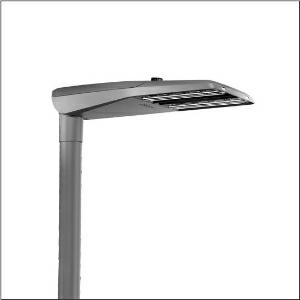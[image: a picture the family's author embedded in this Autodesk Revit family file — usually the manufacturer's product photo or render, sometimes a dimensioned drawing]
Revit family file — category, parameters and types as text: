
# Revit family: streetlight_sl_11_iq_midi___st1_2a_5xc3a41u08me_4bff
name_source: partatom
category: Lighting Fixtures
units: mm (PartAtom-declared; Revit-internal decimal feet)

## family parameters
Cut with Voids When Loaded = No
Host = Face
Light Source = No
Part Type = Normal
Room Calculation Point = No
Round Connector Dimension = Use Diameter
Shared = No

## types (1)
- --- (1 x LED, 18900 lm, 122.6 W, 4000K)
    Apparent Load = 123 VA
    CIE Flux Codes = 32 70 96 100 100
    Color Rendering = 70
    Color Temperature = 4000K
    Default Elevation = 1800 mm
    Description = Streetlight SL 11 iQ midi, mast luminaire, primary light control with 3 zone facetted reflector, of plastic, silver coated, highly specular, primary optical cover: cover, of PMMA, transparent, light distribution: ST1.2a, light emission: direct distribution, primary light characteristic: asymmetric, installation type: post-top, side-entry, lamps: LED, High Power LED, rated values: 18.900lm | 122,6W | 154,2lm/W (begin service life); end service life: 18.900lm | 130,2W; at 50% lumin. flux: 9.450lm | 56,3W | 167,9lm/W, colour temperature: 4000K, colour rendering: CRI > 70, light colour: 740, light setting 1 begin service life: 100% | 18.900lm | 122,6W | 154,2lm/W | 4.000K, light setting 1 end service life: 130,2W, further light settings possible, control: pre-setting: logarithmic dimming characteristic, Street-Remote, Auto-Match, Temp-Guard, Lumen-Switch, Night-Set, Smart-Wire, Light-Fading, Desk-Remote (wireless, voltage-free reading and setting of iQ features in the workshop via application-optimized NFC function/RFID function), optimised constant luminous flux control (CLO 2.0), with cable H07RN-F 5x 1.5mm², mains connection: 230..240V, AC, 50/60Hz, connection cable pre-assembled, cable length: 12,5m, luminaire housing, of diecast aluminium, powder-coated, Siteco® metallic grey (DB 702S), please order mast flange separately, inclination adjustable without tools: 0°, 5°, 10°, 15° (post-top) | 0°, -5°, -10°, -15° (side-entry), sealing non-destructively replaceable, multi-level sealing system, length: 780mm, width: 376mm, height: 118mm, mast flange for spigot size: 42mm (side-entry): 5XC10008XM4, 60/48mm (side-entry/post-top): 5XC10108XM2, 76/60mm (side-entry/post-top): 5XC10108XM1, equipment: Power, Smart Interface below, protection rating (complete): IP66, insulation class (complete): insulation class II (safety insulation), certification: CE, ENEC, ENEC+, VDE, UKCA, impact resistance: IK10, permissible operating ambient temperature for outdoor applications: -25..+50°C, standard-compliant lighting for roads and squares, Environmental Product Declaration (EPD) tested and certified by an independent institute, packaging unit: 1 piece

Light Distribution: ST1.2a
    Height = 118 mm
    Lamp = 1 x LED
    Lamp Light Flux = 18900 lm
    Lamp Power = 122.6 W
    Lamp count = 1
    Length = 780 mm
    Luminous efficacy = 154 lm/W
    Manufacturer = Siteco
    ModVariant = No
    Model = 5XC3A41U08ME
    Number of Poles = 1
    OnlyDefault = Yes
    Power Factor = 1
    Product Name = Streetlight SL 11 iQ midi | ST1.2a
    Product group = mast luminaire | pylon top
    ProductGroupID = 6100
    Protection Class = Protection class II
    Protection Degree = IP 66
    RLX_Detail_Level = 1
    RLX_Emergency_Light_Flux = 0 lm
    RLX_Emergency_Type = 0
    RLX_Emergency_Type_DB = No
    RlxData = <blob elided: 70057 chars, md5=fd2024de>
    Socket = socket
    Standby Power = 0 W
    System Light Flux = 18900 lm
    System Power = 123 W
    Type Comments = factory setting: luminous flux: 100 % | dim-lin: 254 | 552 mA
    Type Image = l_1005968.jpg
    URL = http://relux.com
    VarID = @adj_133076
    Voltage = 0 V
    Weight = 0.00 kg
    Width = 376 mm

## geometry (parser evidence)
native form markers: Blend x4, Sweep x8
no freeform markers — native parametric forms only
